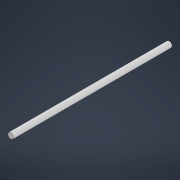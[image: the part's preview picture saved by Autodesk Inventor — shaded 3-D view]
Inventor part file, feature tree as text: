
AUTODESK INVENTOR PART (.ipt)
format: ipt  version: 2021 (Build 250183000, 183)  size: 89,600 bytes
history: native  units: mm
features: extrude x2, sketch x2
ambient origin geometry x8: Origin, YZ Plane, XZ Plane, XY Plane, X Axis, Y Axis, Z Axis, Center Point
bodies: Solid1 (feature_tree)
feature tree (4):
  extrude  "Extrusion1"  Depth=140.0mm TaperAngle=0.0deg
  extrude  "Extrusion2"  Depth=40.0mm TaperAngle=0.0deg
  sketch  "Sketch1"  dims[d0=6.35mm d1=140.0mm d2=0.0mm]
  sketch  "Sketch2"  dims[d3=6.35mm d4=40.0mm d5=0.0mm]
